# Revit family: Sanitary_Toilets_TOTO-USA-Inc_AquiaR-IV-Toilet-1-28-GPF-0-8-GPF-Elonga
name_source: partatom
category: Plumbing Fixtures
revit_build: Autodesk Revit 2015 (Build: 20140606_1530(x64)
units: mm (PartAtom-declared; Revit-internal decimal feet)

## types (1)
- CST446CEMFG
    BIMobject category = Toilets
    BIMobject category code = sanitary-toilets
    BIMobject main category = Sanitary
    BIMobject main category code = sanitary
    Brand url = https://www.totousa.com
    Edition number = 1
    IFC Classification = Flow Terminal
    Installation instructions = https://www.totousa.com
    Manufacturer name = TOTO USA Inc
    Masterformat 2014 Code = 10 28 00
    Masterformat 2014 Description = Toilet, Bath, and Laundry Accessories
    Nominal height = 0 mm  [stored 0 ft]
    Nominal width = 0 mm  [stored 0 ft]
    OmniClass Code = 23-31 19 00
    OmniClass Description = Toilets
    Product Guid = 2e1d9406-196a-45d3-a162-91c8dde85a8d
    Product SKU = toto-cst446cemfg
    Product certification = https://www.totousa.com
    Product data url = https://bimobject.com
    Product family = Urinals
    Product group = Aquia??
    Product url = https://www.totousa.com
    QR code = http://bimobject.com
    Rough-in = 305 mm
    Shipping Weight = 85.00 lbf
    Technical description = https://www.totousa.com
    Trap Seal = 54 mm  [stored 0.177165 ft]
    Trap diameter = 64 mm
    UNSPSC Code = 30181505
    Uniclass 1.4 Code = L7216
    Uniclass 1.4 Description = Toilets
    Uniclass 2.0 Code = SS-35-65-90
    Uniclass 2.0 Description = Toilet Systems
    Uniclass 2015 Code = SL_35_80_89
    Uniclass 2015 Name = Toilets
    Uniformat II Code = D2030
    Uniformat II Description = Sanitary Waste
    Warranty = One year limited

note: [stored X ft] marks values corroborated as IEEE doubles in the binary element streams (Revit-internal decimal feet)

## geometry (parser evidence)
native form markers: Sweep x2
no freeform markers — native parametric forms only
